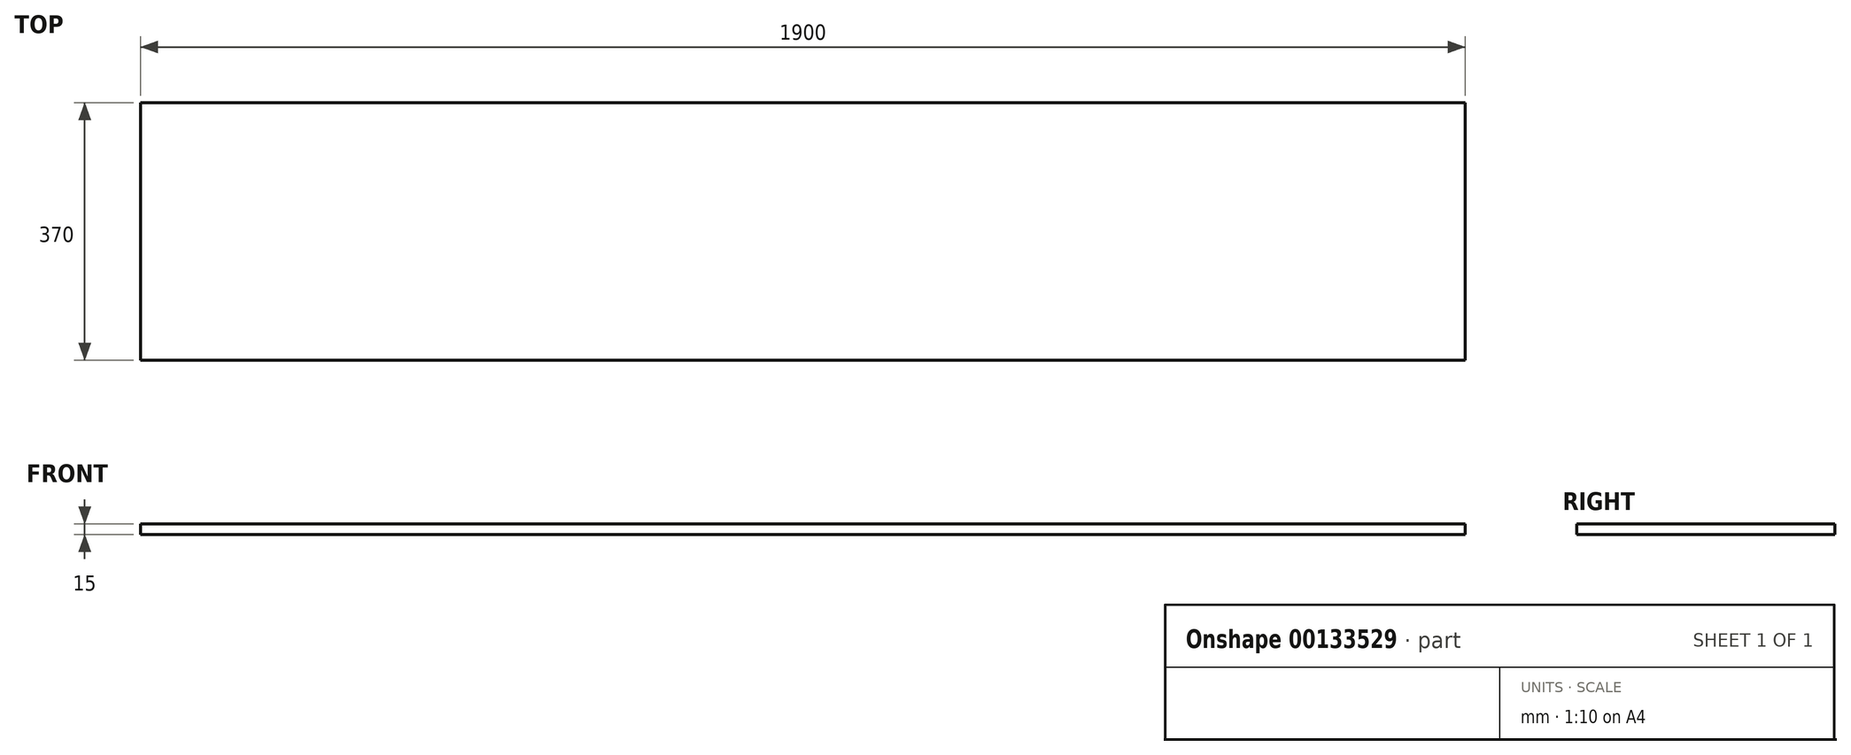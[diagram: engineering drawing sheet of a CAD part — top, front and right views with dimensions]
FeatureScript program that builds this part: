
annotation { "Feature Type Name" : "Feature", "Feature Type Description" : "" }
export const myFeature = defineFeature(function(context is Context, id is Id, definition is map)
    precondition{}
    {
        {
            var Q0;
            Q0=qCreatedBy(makeId("Right.planeOp"),FACE);
            var sketch = newSketch(context, id + "F0", { "sketchPlane" : qUnion([Q0])});
            skLineSegment(sketch, "E0.bottom", {"start": v(185, -7.5) * mm, "end": v(-185, -7.5) * mm});
            skLineSegment(sketch, "E0.top", {"start": v(185, 7.5) * mm, "end": v(-185, 7.5) * mm});
            skLineSegment(sketch, "E0.left", {"start": v(185, -7.5) * mm, "end": v(185, 7.5) * mm});
            skLineSegment(sketch, "E0.right", {"start": v(-185, -7.5) * mm, "end": v(-185, 7.5) * mm});
            skPoint(sketch, "E0.middle", {"position": v(0, 0) * mm});
            skSolve(sketch);
        }
        {
            var Q0;
            Q0 = qSketchRegion(id + "F0", true);
            extrude(context, id + "F1", {"entities" : qUnion([Q0]), "depth" : 1900 * mm});
        }
    });
